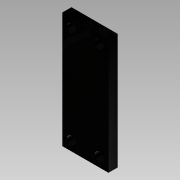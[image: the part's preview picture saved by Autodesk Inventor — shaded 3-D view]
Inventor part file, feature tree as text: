
AUTODESK INVENTOR PART (.ipt)
format: ipt  version: 2015 SP1 (Build 190203100, 203)  size: 103,424 bytes
history: native  units: mm
features: extrude x1, sketch x1
ambient origin geometry x8: Origin, YZ Plane, XZ Plane, XY Plane, X Axis, Y Axis, Z Axis, Center Point
bodies: Solid1 (feature_tree)
feature tree (2):
  extrude  "Extrusion1"  Depth=10.0mm
  sketch  "Sketch1"  dims[d0=25.0mm d1=10.0mm d3=2.0mm d4=2.0mm d5=2.0mm d6=2.0mm d7=2.0mm d8=2.0mm d9=2.0mm d10=2.0mm d11=2.0mm d12=0.0mm d13=2.0mm d14=2.0mm d15=2.0mm d16=2.0mm d17=6.0mm d18=21.0mm]
